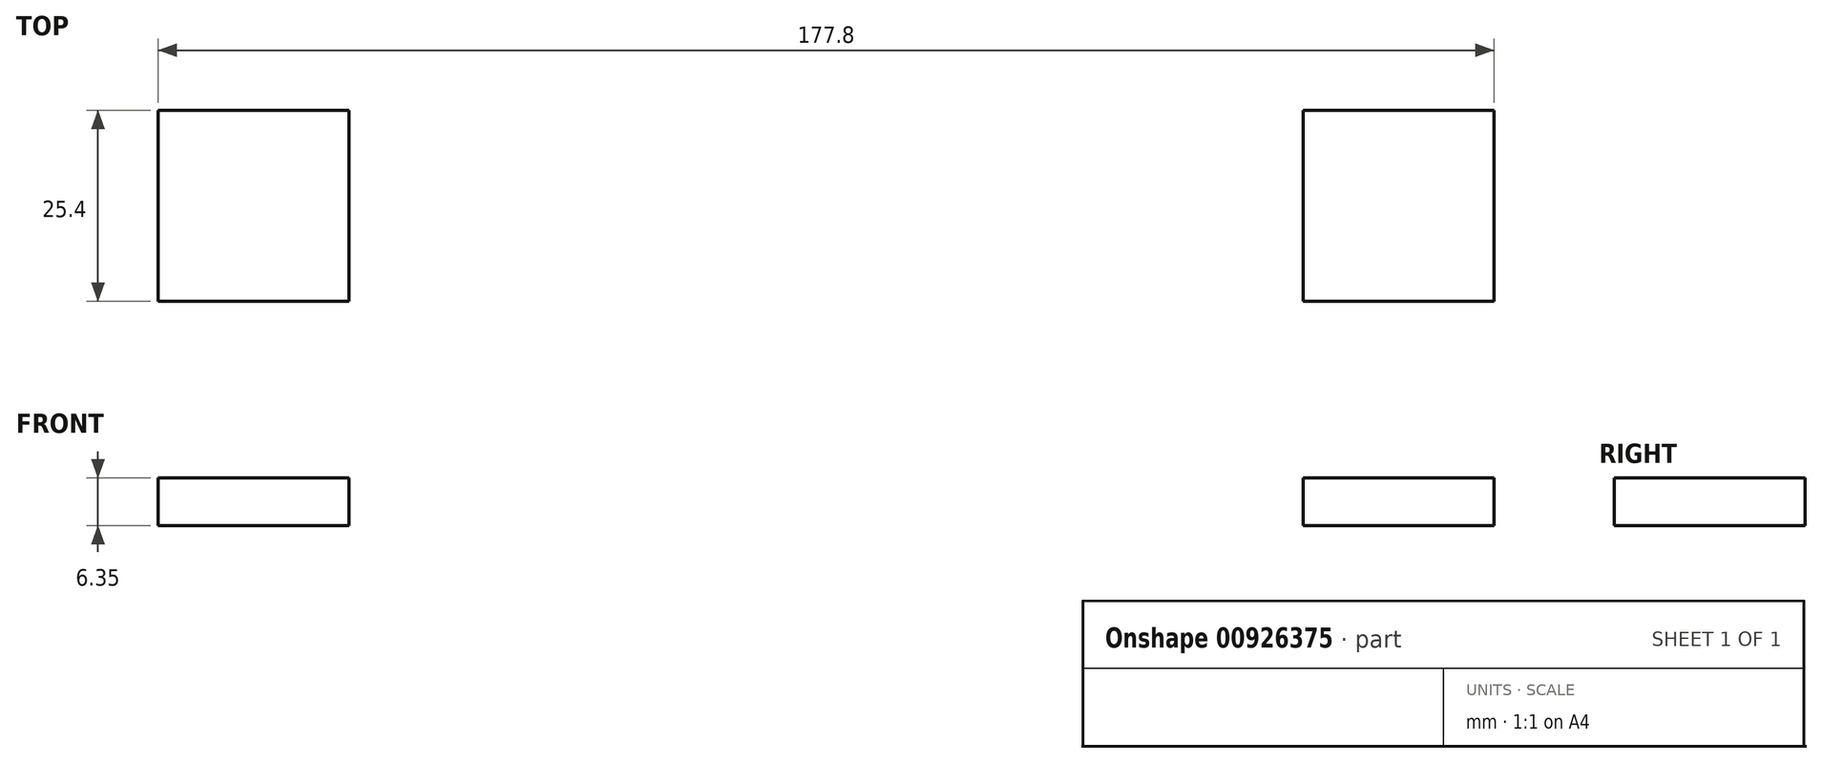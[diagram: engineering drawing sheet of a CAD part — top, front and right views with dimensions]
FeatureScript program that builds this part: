
annotation { "Feature Type Name" : "Feature", "Feature Type Description" : "" }
export const myFeature = defineFeature(function(context is Context, id is Id, definition is map)
    precondition{}
    {
        {
            var Q0;
            Q0=qCreatedBy(makeId("Front.planeOp"),FACE);
            var sketch = newSketch(context, id + "F0", { "sketchPlane" : qUnion([Q0])});
            skLineSegment(sketch, "E0.bottom", {"start": v(-66.63, -2.06) * mm, "end": v(60.37, -2.06) * mm});
            skLineSegment(sketch, "E0.top", {"start": v(-66.63, -14.76) * mm, "end": v(60.37, -14.76) * mm});
            skLineSegment(sketch, "E0.left", {"start": v(-66.63, -2.06) * mm, "end": v(-66.63, -14.76) * mm});
            skLineSegment(sketch, "E0.right", {"start": v(60.37, -2.06) * mm, "end": v(60.37, -14.76) * mm});
            skLineSegment(sketch, "E1", {"start": v(-66.63, 23.55) * mm, "end": v(60.37, 23.55) * mm});
            skLineSegment(sketch, "E2", {"start": v(-46.58, -14.76) * mm, "end": v(-46.58, -40.16) * mm});
            skLineSegment(sketch, "E3", {"start": v(40.32, -14.76) * mm, "end": v(40.32, -40.16) * mm});
            skLineSegment(sketch, "E4.bottom", {"start": v(-66.63, -8.41) * mm, "end": v(-92.03, -8.41) * mm});
            skLineSegment(sketch, "E4.top", {"start": v(-66.63, -14.76) * mm, "end": v(-92.03, -14.76) * mm});
            skLineSegment(sketch, "E4.left", {"start": v(-66.63, -8.41) * mm, "end": v(-66.63, -14.76) * mm});
            skLineSegment(sketch, "E4.right", {"start": v(-92.03, -8.41) * mm, "end": v(-92.03, -14.76) * mm});
            skPoint(sketch, "E5.oppositeSnap0", {"position": v(-79.33, -14.76) * mm});
            skLineSegment(sketch, "E5.bottom", {"start": v(60.37, -8.41) * mm, "end": v(85.77, -8.41) * mm});
            skLineSegment(sketch, "E5.top", {"start": v(60.37, -14.76) * mm, "end": v(85.77, -14.76) * mm});
            skLineSegment(sketch, "E5.left", {"start": v(60.37, -8.41) * mm, "end": v(60.37, -14.76) * mm});
            skLineSegment(sketch, "E5.right", {"start": v(85.77, -8.41) * mm, "end": v(85.77, -14.76) * mm});
            skLineSegment(sketch, "E6", {"start": v(40.32, -40.16) * mm, "end": v(60.37, -14.76) * mm});
            skLineSegment(sketch, "E7", {"start": v(-46.58, -40.16) * mm, "end": v(-66.63, -14.76) * mm});
            skPoint(sketch, "E8", {"position": v(-3.13, -40.16) * mm});
            skLineSegment(sketch, "E9", {"start": v(-46.58, -40.16) * mm, "end": v(-3.13, -40.16) * mm});
            skLineSegment(sketch, "E10", {"start": v(40.32, -40.16) * mm, "end": v(-3.13, -40.16) * mm});
            skPoint(sketch, "E11", {"position": v(-24.85, -40.16) * mm});
            skPoint(sketch, "E12", {"position": v(18.6, -40.16) * mm});
            skPoint(sketch, "E13", {"position": v(-3.13, -14.76) * mm});
            skPoint(sketch, "E14", {"position": v(-24.85, -14.76) * mm});
            skPoint(sketch, "E15", {"position": v(18.6, -14.76) * mm});
            skLineSegment(sketch, "E16", {"start": v(-46.58, -40.16) * mm, "end": v(-24.85, -14.76) * mm});
            skLineSegment(sketch, "E17", {"start": v(-3.13, -40.16) * mm, "end": v(-24.85, -14.76) * mm});
            skLineSegment(sketch, "E18", {"start": v(-3.13, -40.16) * mm, "end": v(18.6, -14.76) * mm});
            skLineSegment(sketch, "E19", {"start": v(18.6, -14.76) * mm, "end": v(40.32, -40.16) * mm});
            skLineSegment(sketch, "E20", {"start": v(-24.85, -40.16) * mm, "end": v(-3.13, -14.76) * mm});
            skLineSegment(sketch, "E21", {"start": v(-3.13, -14.76) * mm, "end": v(18.6, -40.16) * mm});
            skLineSegment(sketch, "E22", {"start": v(40.32, -14.76) * mm, "end": v(18.6, -40.16) * mm});
            skLineSegment(sketch, "E23", {"start": v(-24.85, -40.16) * mm, "end": v(-46.58, -14.76) * mm});
            skLineSegment(sketch, "E24", {"start": v(-24.85, -14.76) * mm, "end": v(-24.85, -40.16) * mm});
            skLineSegment(sketch, "E25", {"start": v(-3.13, -40.16) * mm, "end": v(-3.13, -14.76) * mm});
            skLineSegment(sketch, "E26", {"start": v(18.6, -14.76) * mm, "end": v(18.6, -40.16) * mm});
            skLineSegment(sketch, "E27", {"start": v(-46.58, -14.76) * mm, "end": v(-46.58, -2.06) * mm});
            skLineSegment(sketch, "E28", {"start": v(-24.85, -14.76) * mm, "end": v(-24.85, -2.06) * mm});
            skLineSegment(sketch, "E29", {"start": v(-3.13, -14.76) * mm, "end": v(-3.13, -2.06) * mm});
            skLineSegment(sketch, "E30", {"start": v(18.6, -14.76) * mm, "end": v(18.6, -2.06) * mm});
            skLineSegment(sketch, "E31", {"start": v(40.32, -14.76) * mm, "end": v(40.32, -2.06) * mm});
            skLineSegment(sketch, "E32", {"start": v(-46.58, -2.06) * mm, "end": v(-66.63, 23.55) * mm});
            skLineSegment(sketch, "E33", {"start": v(-24.85, 23.55) * mm, "end": v(-46.58, -2.06) * mm});
            skLineSegment(sketch, "E34", {"start": v(-24.85, 23.55) * mm, "end": v(-3.13, -2.06) * mm});
            skLineSegment(sketch, "E35", {"start": v(-3.13, -2.06) * mm, "end": v(18.6, 23.55) * mm});
            skLineSegment(sketch, "E36", {"start": v(18.6, 23.55) * mm, "end": v(40.32, -2.06) * mm});
            skLineSegment(sketch, "E37", {"start": v(60.37, 23.55) * mm, "end": v(40.32, -2.06) * mm});
            skLineSegment(sketch, "E38", {"start": v(-66.63, 23.55) * mm, "end": v(-92.03, -8.41) * mm});
            skLineSegment(sketch, "E39", {"start": v(60.37, 23.55) * mm, "end": v(85.77, -8.41) * mm});
            skSolve(sketch);
        }
        {
            var Q0;
            Q0=makeQuery(id+"F0.imprint","IMPRINT",FACE,{"disambiguationData":[TD([[makeQuery(id+"F0.imprint","IMPRINT",EDGE,{"derivedFrom":sQuery(id+"F0.wireOp",EDGE,"E4.bottom")}),1.0]])]});
            var Q1;
            Q1=makeQuery(id+"F0.imprint","IMPRINT",FACE,{"disambiguationData":[TD([[makeQuery(id+"F0.imprint","IMPRINT",EDGE,{"derivedFrom":sQuery(id+"F0.wireOp",EDGE,"E5.bottom")}),-1.0]])]});
            extrude(context, id + "F1", {"entities" : qUnion([Q0, Q1]), "endBound" : BoundingType.SYMMETRIC, "depth" : 25.4 * mm, "offsetDistance" : 25.4 * mm});
        }
    });
